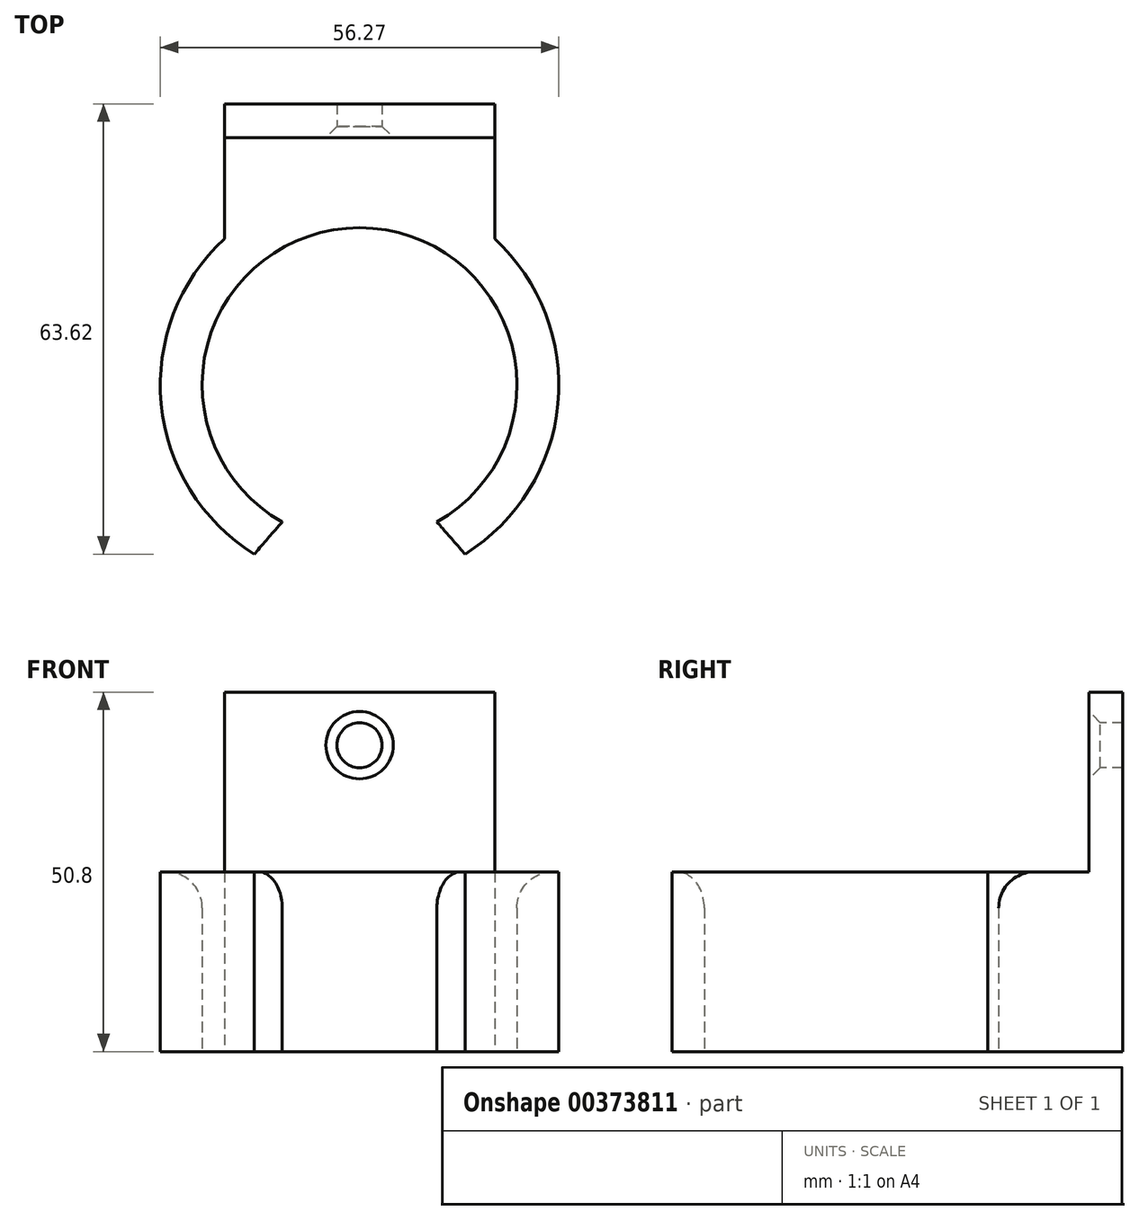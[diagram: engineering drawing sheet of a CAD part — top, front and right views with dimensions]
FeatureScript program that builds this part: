
annotation { "Feature Type Name" : "Feature", "Feature Type Description" : "" }
export const myFeature = defineFeature(function(context is Context, id is Id, definition is map)
    precondition{}
    {
        {
            var Q0;
            Q0=qCreatedBy(makeId("Top.planeOp"),FACE);
            var sketch = newSketch(context, id + "F0", { "sketchPlane" : qUnion([Q0])});
            skLineSegment(sketch, "E0.bottom", {"start": v(-64.42, 59.25) * mm, "end": v(-26.28, 59.25) * mm});
            skLineSegment(sketch, "E0.left", {"start": v(-64.42, 59.25) * mm, "end": v(-64.42, 40.2) * mm});
            skLineSegment(sketch, "E0.right", {"start": v(-26.28, 59.25) * mm, "end": v(-26.28, 40.2) * mm});
            skArc(sketch, "E1", {"start": v(-64.42, 40.2) * mm, "mid": v(-73.36, 16.87) * mm, "end": v(-60.22, -4.37) * mm});
            skArc(sketch, "E2", {"start": v(-30.47, -4.37) * mm, "mid": v(-45.35, 47.65) * mm, "end": v(-60.22, -4.37) * mm});
            skArc(sketch, "E3", {"start": v(-34.42, 0.16) * mm, "mid": v(-45.35, 41.74) * mm, "end": v(-56.28, 0.16) * mm});
            skPoint(sketch, "E4", {"position": v(-56.28, 0.16) * mm});
            skPoint(sketch, "E5", {"position": v(-60.22, -4.37) * mm});
            skPoint(sketch, "E6.MirrorP", {"position": v(-34.42, 0.16) * mm});
            skPoint(sketch, "E7.MirrorP", {"position": v(-30.47, -4.37) * mm});
            skArc(sketch, "E8.trimOffspring", {"start": v(-30.47, -4.37) * mm, "mid": v(-17.33, 16.87) * mm, "end": v(-26.28, 40.2) * mm});
            skPoint(sketch, "E9.orphan", {"position": v(-45.35, 59.25) * mm});
            skLineSegment(sketch, "E10", {"start": v(-56.28, 0.16) * mm, "end": v(-60.22, -4.37) * mm});
            skLineSegment(sketch, "E11", {"start": v(-34.42, 0.16) * mm, "end": v(-30.47, -4.37) * mm});
            skLineSegment(sketch, "E12.left", {"start": v(-64.42, 59.25) * mm, "end": v(-64.42, 49.72) * mm});
            skLineSegment(sketch, "E12.right", {"start": v(-26.28, 59.25) * mm, "end": v(-26.28, 49.72) * mm});
            skPoint(sketch, "E13.end.orphan", {"position": v(-64.42, 54.49) * mm});
            skPoint(sketch, "E13.start.orphan", {"position": v(-26.28, 54.49) * mm});
            skLineSegment(sketch, "E14.bottom", {"start": v(-64.42, 54.49) * mm, "end": v(-26.28, 54.49) * mm});
            skLineSegment(sketch, "E14.left", {"start": v(-64.42, 54.49) * mm, "end": v(-64.42, 59.25) * mm});
            skLineSegment(sketch, "E14.right", {"start": v(-26.28, 54.49) * mm, "end": v(-26.28, 59.25) * mm});
            skPoint(sketch, "E14.top.end.orphan", {"position": v(-26.28, 63.99) * mm});
            skSolve(sketch);
        }
        {
            var Q0;
            {var subQ1=sQuery(id+"F0.wireOp",EDGE,"E0.left");Q0=makeQuery(id+"F0.imprint","IMPRINT",FACE,{"disambiguationData":[TD([[makeQuery(id+"F0.imprint","IMPRINT",EDGE,{"derivedFrom":subQ1}),1.0]])]});}
            var Q1;
            Q1=makeQuery(id+"F0.imprint","IMPRINT",FACE,{"disambiguationData":[TD([[makeQuery(id+"F0.imprint","IMPRINT",EDGE,{"derivedFrom":sQuery(id+"F0.wireOp",EDGE,"E3")}),-1.0]])]});
            extrude(context, id + "F1", {"entities" : qUnion([Q0, Q1]), "depth" : 25.4 * mm});
        }
        {
            var Q0;
            {var subQ0=sQuery(id+"F0.wireOp",EDGE,"E0.bottom");Q0=makeQuery(id+"F0.imprint","IMPRINT",FACE,{"disambiguationData":[TD([[makeQuery(id+"F0.imprint","IMPRINT",EDGE,{"derivedFrom":subQ0}),-1.0]])]});}
            extrude(context, id + "F2", {"entities" : qUnion([Q0]), "operationType" : NewBodyOperationType.ADD, "depth" : 50.8 * mm});
        }
        {
            var Q0;
            Q0=makeQuery(id+"F2.opExtrude","SWEPT_FACE",FACE,{"disambiguationData":[OSD([sQuery(id+"F0.wireOp",EDGE,"E14.bottom")])]});
            var sketch = newSketch(context, id + "F3", { "sketchPlane" : qUnion([Q0])});
            skPoint(sketch, "E15", {"position": v(-45.35, 43.3) * mm});
            skPoint(sketch, "E15.positionSnap0", {"position": v(-45.35, 25.4) * mm});
            skSolve(sketch);
        }
        {
            var Q0;
            Q0=sQuery(id+"F3.wireOp",VERTEX,"E15");
            var Q1;
            Q1=makeQuery(id+"F1.opExtrude","SWEPT_BODY",BODY,{"disambiguationData":[OSD([sQuery(id+"F0.wireOp",EDGE,"E0.left"),sQuery(id+"F0.wireOp",EDGE,"E0.right"),sQuery(id+"F0.wireOp",EDGE,"E2"),sQuery(id+"F0.wireOp",EDGE,"E3"),sQuery(id+"F0.wireOp",EDGE,"E8.trimOffspring"),sQuery(id+"F0.wireOp",EDGE,"E10"),sQuery(id+"F0.wireOp",EDGE,"E11"),sQuery(id+"F0.wireOp",EDGE,"E12.left"),sQuery(id+"F0.wireOp",EDGE,"E12.right"),sQuery(id+"F0.wireOp",EDGE,"E14.bottom")])]});
            hole(context, id + "F4", {"style" : HoleStyle.C_SINK, "endStyle" : HoleEndStyle.THROUGH, "holeDiameter" : 6.35 * mm, "cSinkDiameter" : 9.52 * mm, "cSinkAngle" : 90 * degree, "majorDiameter" : 5 * mm, "isTappedThrough" : true, "tappedDepth" : 12.7 * mm, "tapClearance" : 3, "locations" : qUnion([Q0]), "scope" : qUnion([Q1])});
        }
        {
            var Q0;
            Q0=makeQuery(id+"F1.opExtrude","CAP_EDGE",EDGE,{"disambiguationData":[OSD([sQuery(id+"F0.wireOp",EDGE,"E3")])],"isStart":false});
            fillet(context, id + "F5", {"entities" : qUnion([Q0]), "radius" : 5.08 * mm, "tangentPropagation" : true, "allowEdgeOverflow" : false});
        }
    });
